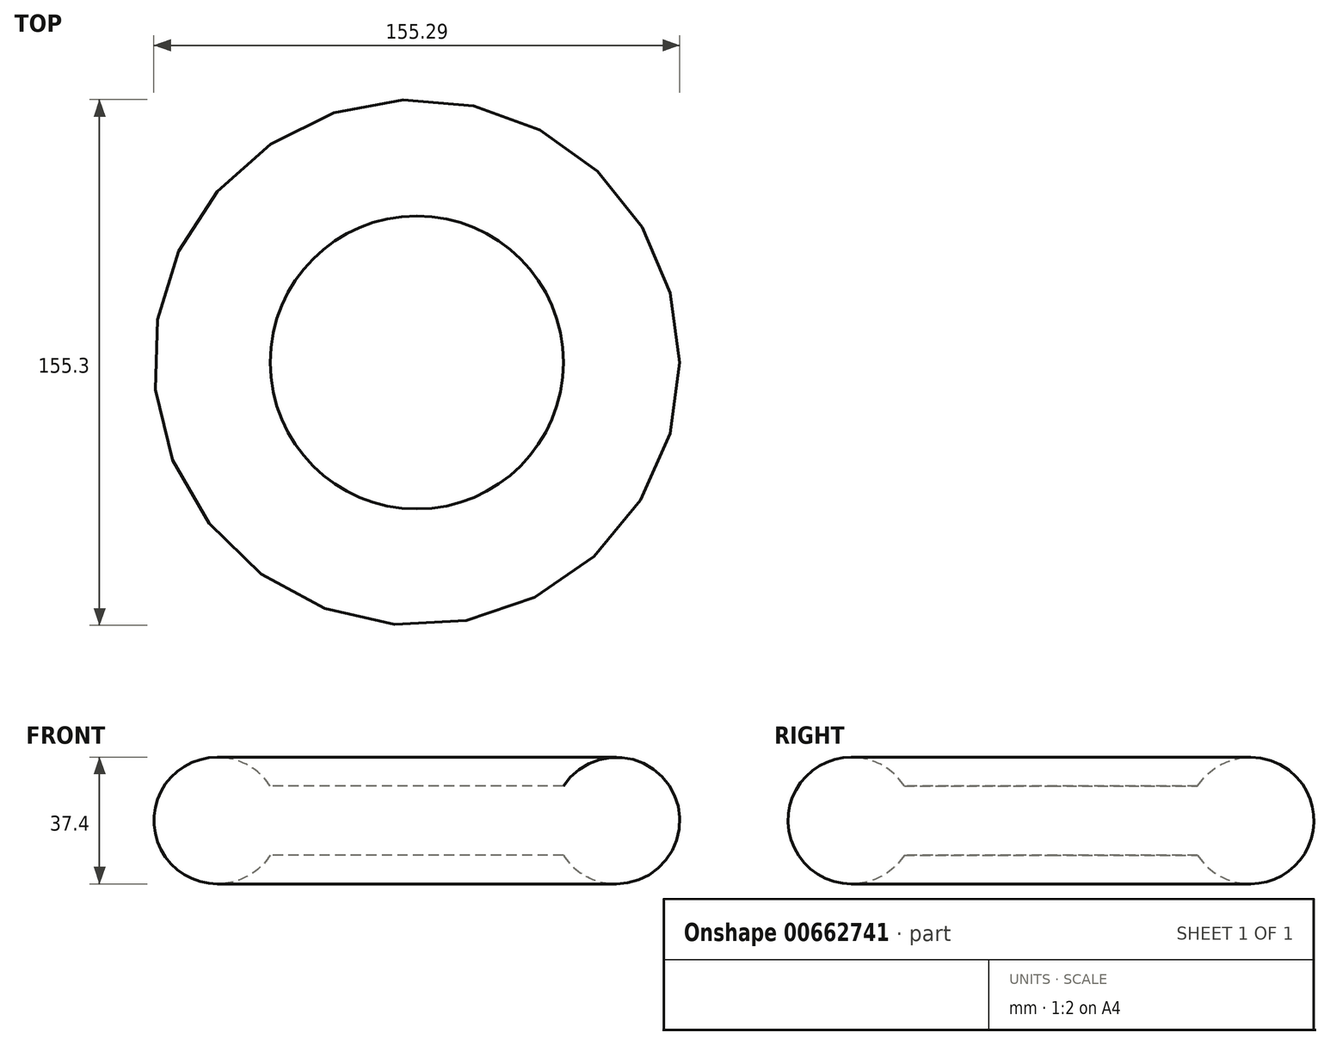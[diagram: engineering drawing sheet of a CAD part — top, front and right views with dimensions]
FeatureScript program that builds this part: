
annotation { "Feature Type Name" : "Feature", "Feature Type Description" : "" }
export const myFeature = defineFeature(function(context is Context, id is Id, definition is map)
    precondition{}
    {
        {
            var Q0;
            Q0=qCreatedBy(makeId("Front.planeOp"),FACE);
            var sketch = newSketch(context, id + "F0", { "sketchPlane" : qUnion([Q0])});
            skLineSegment(sketch, "E0.bottom", {"start": v(-21.64, 10.23) * mm, "end": v(21.64, 10.23) * mm});
            skLineSegment(sketch, "E0.top", {"start": v(-21.64, -10.23) * mm, "end": v(21.64, -10.23) * mm});
            skLineSegment(sketch, "E0.left", {"start": v(-21.64, 10.23) * mm, "end": v(-21.64, -10.23) * mm});
            skPoint(sketch, "E0.middle", {"position": v(0, 0) * mm});
            skArc(sketch, "E1", {"start": v(21.64, -10.23) * mm, "mid": v(56, 0) * mm, "end": v(21.64, 10.23) * mm});
            skSolve(sketch);
        }
        {
            var Q0;
            Q0=makeQuery(id+"F0.imprint","IMPRINT",FACE,{"disambiguationData":[TD([[makeQuery(id+"F0.imprint","IMPRINT",EDGE,{"derivedFrom":sQuery(id+"F0.wireOp",EDGE,"E0.bottom")}),-1.0]])]});
            var Q1;
            Q1=sQuery(id+"F0.wireOp",EDGE,"E0.left");
            revolve(context, id + "F1", {"entities" : qUnion([Q0]), "axis" : qUnion([Q1]), "revolveType" : RevolveType.FULL});
        }
    });
